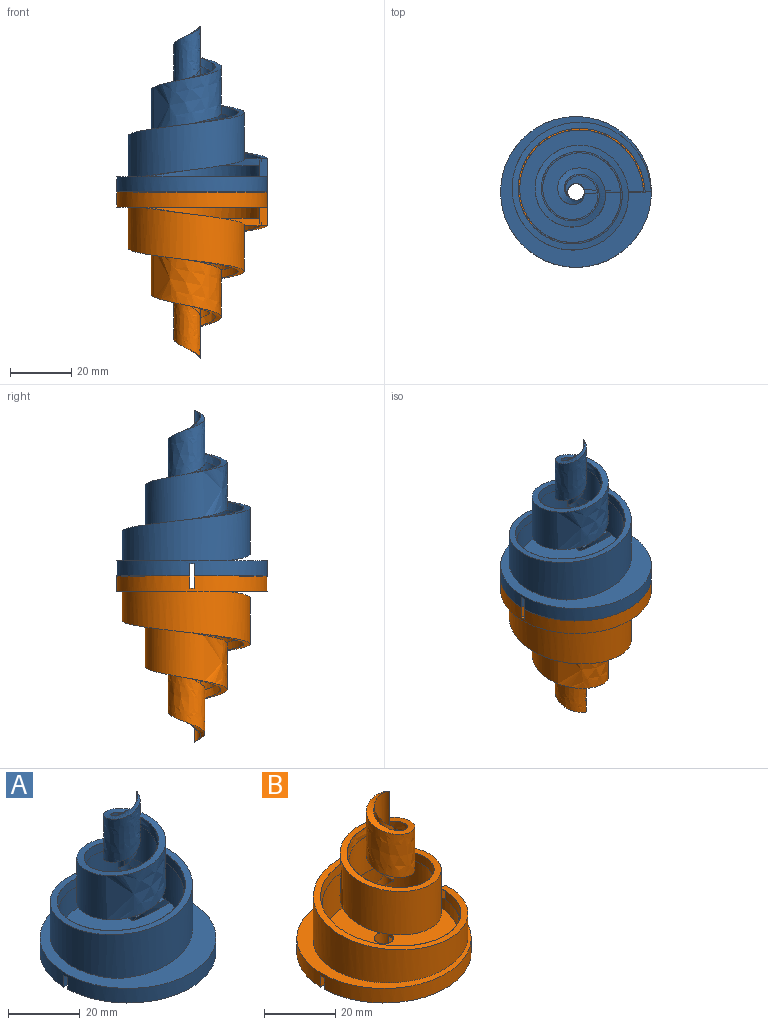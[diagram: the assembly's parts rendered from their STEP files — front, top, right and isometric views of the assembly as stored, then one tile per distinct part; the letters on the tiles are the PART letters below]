
ASSEMBLY  parts=2 mates=1
PART A: 21 faces, bbox 53x53x62.2 mm
  f0: plane 48.98x23.75mm, normal (0,0,-1), area 898.3mm2, adj f8,f9,f17,f19
  f1: bspline ~45.29x43.16mm, area 487mm2, adj f3,f5,f7,f12
  f2: offset ~53.82x42.26mm, area 2148.5mm2, adj f4,f6,f7,f11,f12
  f3: offset ~62x45.22mm, area 3360.8mm2, adj f1,f4,f6,f7,f11,f12
  f4: bspline ~19.94x2.49mm, area 48.7mm2, adj f2,f3,f5,f6,f7,f14
  f5: bspline ~42.39x41.3mm, area 4.6mm2, adj f1,f4,f7,f12
  f6: bspline ~33.19x18.94mm, area 109.4mm2, adj f2,f3,f4,f11
  f7: plane 6x2.5mm, normal (0.05,-1,0), area 14.6mm2, adj f1,f2,f3,f4,f5,f11
  f8: cylinder r=2.75mm len=5.5mm, axis (0,0,1), area 74.2mm2, adj f0,f10,f11,f15,f16,f17,f18,f19
  f9: cylinder r=24.5mm len=49mm, axis (0,0,1), area 757.7mm2, adj f0,f10,f11,f15,f16,f17,f18,f19
  f10: plane 48.98x23.75mm, normal (0,0,-1), area 898.3mm2, adj f8,f9,f16,f20
  f11: plane 49x49mm, normal (0,0,1), area 1663.9mm2, adj f2,f3,f6,f7,f8,f9
  f12: cylinder r=2.75mm len=22.59mm, axis (0,0,-1), area 156mm2, adj f1,f2,f3,f5,f13
  f13: cylinder r=2.75mm len=18.35mm, axis (0,0,-1), area 57.8mm2, adj f12,f14
  f14: cylinder r=2.75mm len=10.88mm, axis (0,0,-1), area 31.8mm2, adj f4,f13
  f15: plane 21.85x1.5mm, normal (0,0,-1), area 32.7mm2, adj f8,f9,f16,f17
  f16: plane 21.84x4mm, normal (0,1,0), area 87.4mm2, adj f8,f9,f10,f15
  f17: plane 21.84x4mm, normal (0,-1,0), area 87.4mm2, adj f0,f8,f9,f15
  f18: plane 21.85x1.5mm, normal (0,0,-1), area 32.7mm2, adj f8,f9,f19,f20
  f19: plane 21.84x4mm, normal (0,-1,0), area 87.4mm2, adj f0,f8,f9,f18
  f20: plane 21.84x4mm, normal (0,1,0), area 87.4mm2, adj f8,f9,f10,f18
PART B: 21 faces, bbox 53x53x62.8 mm
  f0: plane 48.98x23.75mm, normal (0,0,-1), area 898.3mm2, adj f8,f9,f17,f19
  f1: bspline ~45.29x43.16mm, area 487.4mm2, adj f2,f5,f7,f12
  f2: offset ~62.81x45.32mm, area 3354.5mm2, adj f1,f4,f6,f7,f11,f12
  f3: offset ~53.82x42.26mm, area 2146.1mm2, adj f4,f6,f7,f11,f12
  f4: bspline ~20.63x2.49mm, area 48.7mm2, adj f2,f3,f5,f6,f7,f14
  f5: bspline ~42.39x41.3mm, area 5.1mm2, adj f1,f4,f7,f12
  f6: bspline ~33.98x21.84mm, area 109.4mm2, adj f2,f3,f4,f11
  f7: plane 6x2.5mm, normal (0.05,1,0), area 14.6mm2, adj f1,f2,f3,f4,f5,f11
  f8: cylinder r=2.75mm len=5.5mm, axis (0,0,1), area 74.2mm2, adj f0,f10,f11,f15,f16,f17,f18,f19
  f9: cylinder r=24.5mm len=49mm, axis (0,0,1), area 757.7mm2, adj f0,f10,f11,f15,f16,f17,f18,f19
  f10: plane 48.98x23.75mm, normal (0,0,-1), area 898.3mm2, adj f8,f9,f16,f20
  f11: plane 49x49mm, normal (0,0,1), area 1663.9mm2, adj f2,f3,f6,f7,f8,f9
  f12: cylinder r=2.75mm len=22.59mm, axis (0,0,-1), area 156mm2, adj f1,f2,f3,f5,f13
  f13: cylinder r=2.75mm len=18.35mm, axis (0,0,-1), area 57.8mm2, adj f12,f14
  f14: cylinder r=2.75mm len=10.88mm, axis (0,0,-1), area 31.8mm2, adj f4,f13
  f15: plane 21.85x1.5mm, normal (0,0,-1), area 32.7mm2, adj f8,f9,f16,f17
  f16: plane 21.84x4mm, normal (0,1,0), area 87.4mm2, adj f8,f9,f10,f15
  f17: plane 21.84x4mm, normal (0,-1,0), area 87.4mm2, adj f0,f8,f9,f15
  f18: plane 21.85x1.5mm, normal (0,0,-1), area 32.7mm2, adj f8,f9,f19,f20
  f19: plane 21.84x4mm, normal (0,-1,0), area 87.4mm2, adj f0,f8,f9,f18
  f20: plane 21.84x4mm, normal (0,1,0), area 87.4mm2, adj f8,f9,f10,f18
PLACE A t=(-2.05,-11.32,99.21)mm
PLACE B rot(axis=(-1,0,0),180deg) t=(-2.05,-11.32,79.21)mm
MATE fastened A.f8 <-> B.f8  axis (0,0,-1) through (-2.05,-11.32,89.21)mm
